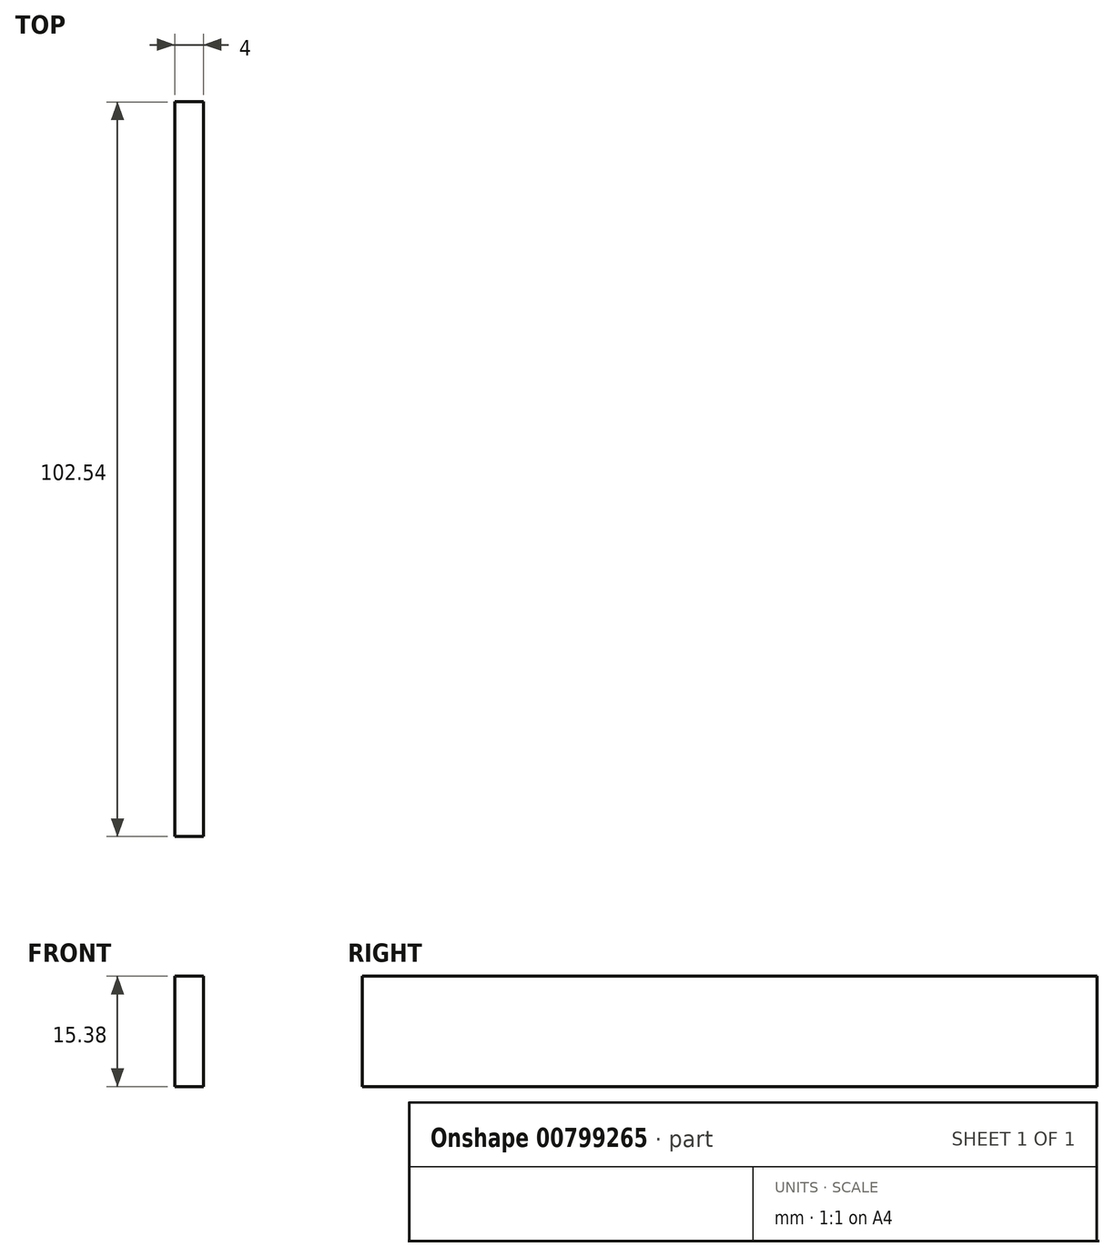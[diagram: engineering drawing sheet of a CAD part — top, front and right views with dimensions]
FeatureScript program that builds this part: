
annotation { "Feature Type Name" : "Feature", "Feature Type Description" : "" }
export const myFeature = defineFeature(function(context is Context, id is Id, definition is map)
    precondition{}
    {
        {
            var Q0;
            Q0=qCreatedBy(makeId("Right.planeOp"),FACE);
            var sketch = newSketch(context, id + "F0", { "sketchPlane" : qUnion([Q0])});
            skLineSegment(sketch, "E0.bottom", {"start": v(-51.27, 7.69) * mm, "end": v(51.27, 7.69) * mm});
            skLineSegment(sketch, "E0.top", {"start": v(-51.27, -7.69) * mm, "end": v(51.27, -7.69) * mm});
            skLineSegment(sketch, "E0.left", {"start": v(-51.27, 7.69) * mm, "end": v(-51.27, -7.69) * mm});
            skLineSegment(sketch, "E0.right", {"start": v(51.27, 7.69) * mm, "end": v(51.27, -7.69) * mm});
            skPoint(sketch, "E0.middle", {"position": v(0, 0) * mm});
            skSolve(sketch);
        }
        {
            var Q0;
            Q0=makeQuery(id+"F0.imprint","IMPRINT",FACE,{"disambiguationData":[TD([[makeQuery(id+"F0.imprint","IMPRINT",EDGE,{"derivedFrom":sQuery(id+"F0.wireOp",EDGE,"E0.bottom")}),-1.0]])]});
            extrude(context, id + "F1", {"entities" : qUnion([Q0]), "depth" : 4 * mm, "offsetDistance" : 25 * mm});
        }
    });
